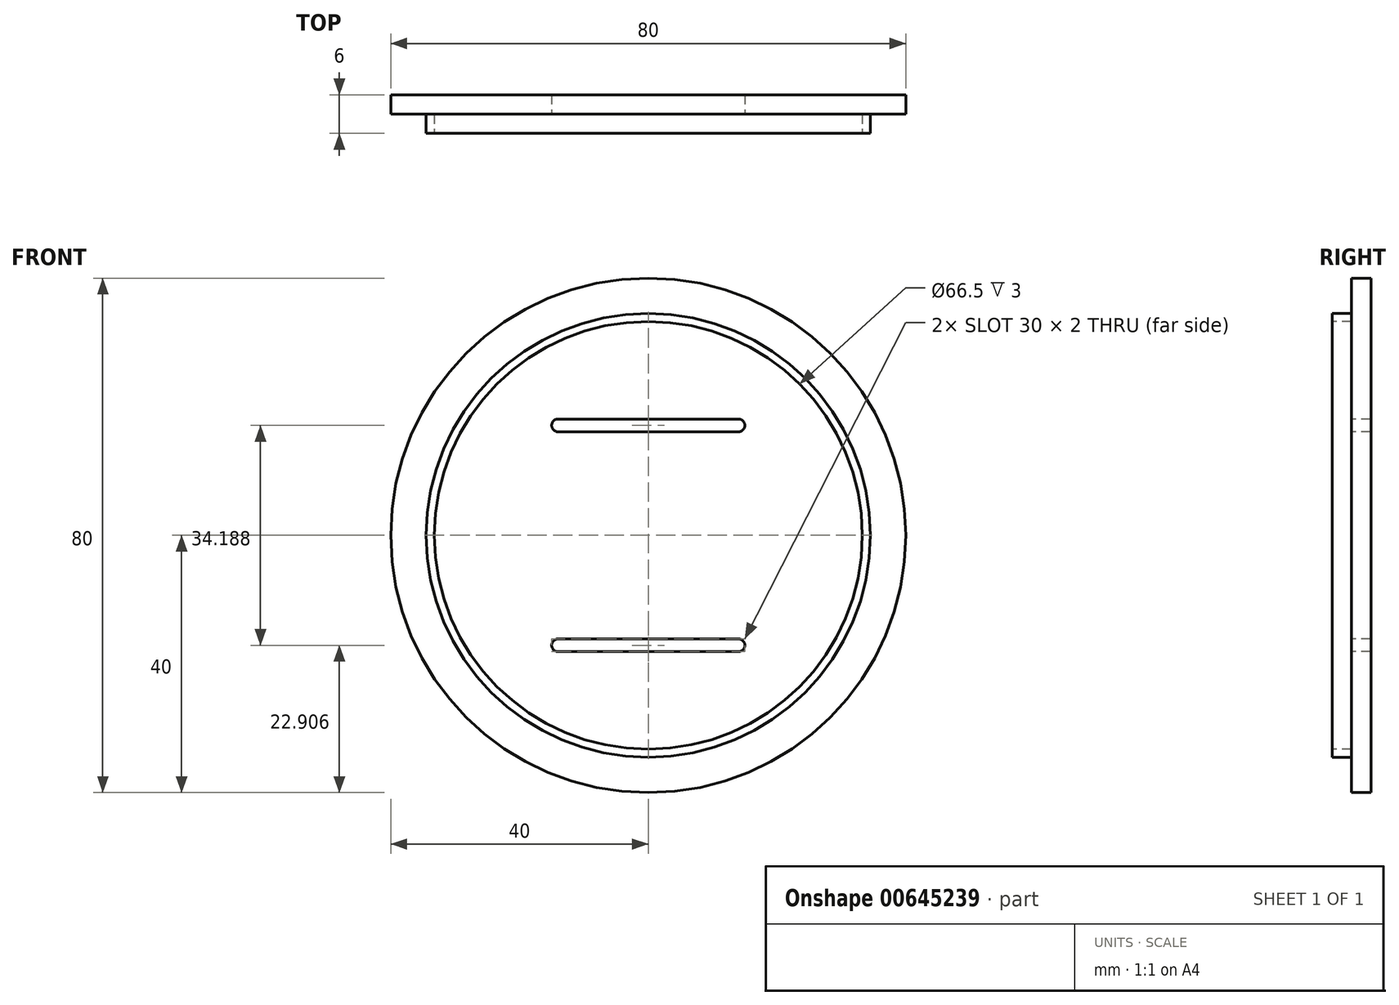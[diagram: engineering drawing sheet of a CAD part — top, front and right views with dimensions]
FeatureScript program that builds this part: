
annotation { "Feature Type Name" : "Feature", "Feature Type Description" : "" }
export const myFeature = defineFeature(function(context is Context, id is Id, definition is map)
    precondition{}
    {
        {
            var Q0;
            Q0=qCreatedBy(makeId("Front.planeOp"),FACE);
            var sketch = newSketch(context, id + "F0", { "sketchPlane" : qUnion([Q0])});
            skCircle(sketch, "E0", {"center": v(0, 0) * mm, "radius": 40 * mm});
            skSolve(sketch);
        }
        {
            var Q0;
            Q0=makeQuery(id+"F0.imprint","IMPRINT",FACE,{"disambiguationData":[TD([[makeQuery(id+"F0.imprint","IMPRINT",EDGE,{"derivedFrom":sQuery(id+"F0.wireOp",EDGE,"E0")}),1.0]])]});
            extrude(context, id + "F1", {"entities" : qUnion([Q0]), "depth" : 3 * mm, "offsetDistance" : 25 * mm});
        }
        {
            var Q0;
            Q0=makeQuery(id+"F1.opExtrude","CAP_FACE",FACE,{"disambiguationData":[OSD([sQuery(id+"F0.wireOp",EDGE,"E0")])],"isStart":false});
            var sketch = newSketch(context, id + "F2", { "sketchPlane" : qUnion([Q0])});
            skCircle(sketch, "E1", {"center": v(0, 0) * mm, "radius": 34.5 * mm});
            skSolve(sketch);
        }
        {
            var Q0;
            Q0=makeQuery(id+"F2.imprint","IMPRINT",FACE,{"disambiguationData":[TD([[makeQuery(id+"F2.imprint","IMPRINT",EDGE,{"derivedFrom":sQuery(id+"F2.wireOp",EDGE,"E1")}),1.0]])]});
            extrude(context, id + "F3", {"entities" : qUnion([Q0]), "operationType" : NewBodyOperationType.ADD, "depth" : 3 * mm, "offsetDistance" : 25 * mm});
        }
        {
            var Q0;
            Q0=makeQuery(id+"F3.opExtrude","CAP_FACE",FACE,{"disambiguationData":[OSD([sQuery(id+"F2.wireOp",EDGE,"E1")])],"isStart":false});
            var sketch = newSketch(context, id + "F4", { "sketchPlane" : qUnion([Q0])});
            skCircle(sketch, "E2", {"center": v(0, 0) * mm, "radius": 33.25 * mm});
            skSolve(sketch);
        }
        {
            var Q0;
            Q0=makeQuery(id+"F4.imprint","IMPRINT",FACE,{"disambiguationData":[TD([[makeQuery(id+"F4.imprint","IMPRINT",EDGE,{"derivedFrom":sQuery(id+"F4.wireOp",EDGE,"E2")}),1.0]])]});
            extrude(context, id + "F5", {"entities" : qUnion([Q0]), "operationType" : NewBodyOperationType.REMOVE, "oppositeDirection" : true, "depth" : 3 * mm, "offsetDistance" : 25 * mm});
        }
        {
            var Q0;
            Q0=makeQuery(id+"F5.boolean.opBoolean","COPY",FACE,{"derivedFrom":makeQuery(id+"F5.opExtrude","CAP_FACE",FACE,{"disambiguationData":[OSD([sQuery(id+"F4.wireOp",EDGE,"E2")])],"isStart":false})});
            var sketch = newSketch(context, id + "F6", { "sketchPlane" : qUnion([Q0])});
            skLineSegment(sketch, "E3.bottom", {"start": v(-14, 18.1) * mm, "end": v(14, 18.1) * mm});
            skLineSegment(sketch, "E3.top", {"start": v(-14, 16.1) * mm, "end": v(14, 16.1) * mm});
            skLineSegment(sketch, "E3.left", {"start": v(-15, 17.1) * mm, "end": v(-15, 17.1) * mm});
            skLineSegment(sketch, "E3.right", {"start": v(15, 17.1) * mm, "end": v(15, 17.1) * mm});
            skPoint(sketch, "E3.middle", {"position": v(0, 17.1) * mm});
            skLineSegment(sketch, "E4", {"start": v(-33.25, 0) * mm, "end": v(33.25, 0) * mm, "construction": true});
            skPoint(sketch, "E5.visualSharp", {"position": v(-15, 18.1) * mm});
            skArc(sketch, "E5.filletArc", {"start": v(-14, 18.1) * mm, "mid": v(-14.7, 17.8) * mm, "end": v(-15, 17.1) * mm});
            skPoint(sketch, "E6.visualSharp", {"position": v(-15, 16.1) * mm});
            skArc(sketch, "E6.filletArc", {"start": v(-15, 17.1) * mm, "mid": v(-14.7, 16.39) * mm, "end": v(-14, 16.1) * mm});
            skPoint(sketch, "E7.visualSharp", {"position": v(15, 18.1) * mm});
            skArc(sketch, "E7.filletArc", {"start": v(15, 17.1) * mm, "mid": v(14.7, 17.8) * mm, "end": v(14, 18.1) * mm});
            skPoint(sketch, "E8.visualSharp", {"position": v(15, 16.1) * mm});
            skArc(sketch, "E8.filletArc", {"start": v(14, 16.1) * mm, "mid": v(14.7, 16.39) * mm, "end": v(15, 17.1) * mm});
            skLineSegment(sketch, "E9.MirrorCS", {"start": v(-14, -16.1) * mm, "end": v(14, -16.1) * mm});
            skArc(sketch, "E10.MirrorCS", {"start": v(-15, -17.1) * mm, "mid": v(-14.7, -16.39) * mm, "end": v(-14, -16.1) * mm});
            skArc(sketch, "E11.MirrorCS", {"start": v(-14, -18.1) * mm, "mid": v(-14.7, -17.8) * mm, "end": v(-15, -17.1) * mm});
            skLineSegment(sketch, "E12.MirrorCS", {"start": v(-14, -18.1) * mm, "end": v(14, -18.1) * mm});
            skPoint(sketch, "E13.MirrorP", {"position": v(15, -18.1) * mm});
            skArc(sketch, "E14.MirrorCS", {"start": v(14, -16.1) * mm, "mid": v(14.7, -16.39) * mm, "end": v(15, -17.1) * mm});
            skArc(sketch, "E15.MirrorCS", {"start": v(15, -17.1) * mm, "mid": v(14.7, -17.8) * mm, "end": v(14, -18.1) * mm});
            skSolve(sketch);
        }
        {
            var Q0;
            Q0=makeQuery(id+"F6.imprint","IMPRINT",FACE,{"disambiguationData":[TD([[makeQuery(id+"F6.imprint","IMPRINT",EDGE,{"derivedFrom":sQuery(id+"F6.wireOp",EDGE,"E3.bottom")}),-1.0]])]});
            var Q1;
            Q1=makeQuery(id+"F6.imprint","IMPRINT",FACE,{"disambiguationData":[TD([[makeQuery(id+"F6.imprint","IMPRINT",EDGE,{"derivedFrom":sQuery(id+"F6.wireOp",EDGE,"E9.MirrorCS")}),-1.0]])]});
            extrude(context, id + "F7", {"entities" : qUnion([Q0, Q1]), "operationType" : NewBodyOperationType.REMOVE, "endBound" : BoundingType.THROUGH_ALL, "oppositeDirection" : true, "depth" : 25 * mm, "offsetDistance" : 25 * mm});
        }
    });
